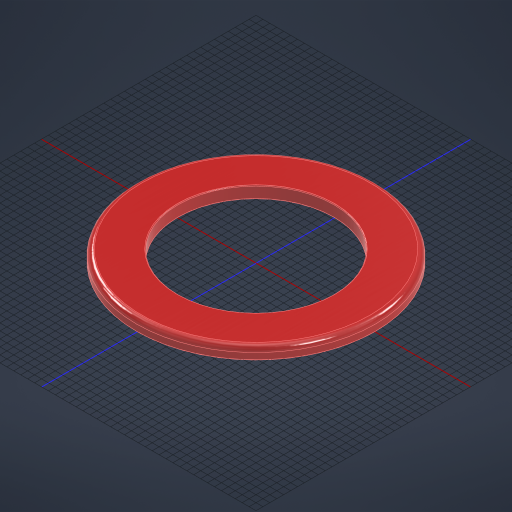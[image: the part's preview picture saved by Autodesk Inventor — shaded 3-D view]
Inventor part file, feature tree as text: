
AUTODESK INVENTOR PART (.ipt)
format: ipt  version: 2023.2 (Build 272271030, 271C)  size: 325,120 bytes
history: native  units: mm
features: fillet x3, extrude x1, sketch x1
ambient origin geometry x8: Origin, YZ Plane, XZ Plane, XY Plane, X Axis, Y Axis, Z Axis, Center Point
bodies: Volumenkörper1 (feature_tree)
feature tree (5):
  extrude  "Extrusion1"  Depth=2.0mm
  fillet  "Rundung1"  Radius=35.0mm
  fillet  "Rundung2"  Radius=15.0mm
  fillet  "Rundung3"  Radius=2.0mm
  sketch  "Skizze1"  dims[d0=120.0mm d1=451.0mm d2=35.0mm d3=0.0mm d4=15.0mm d5=2.0mm d6=2.0mm]
